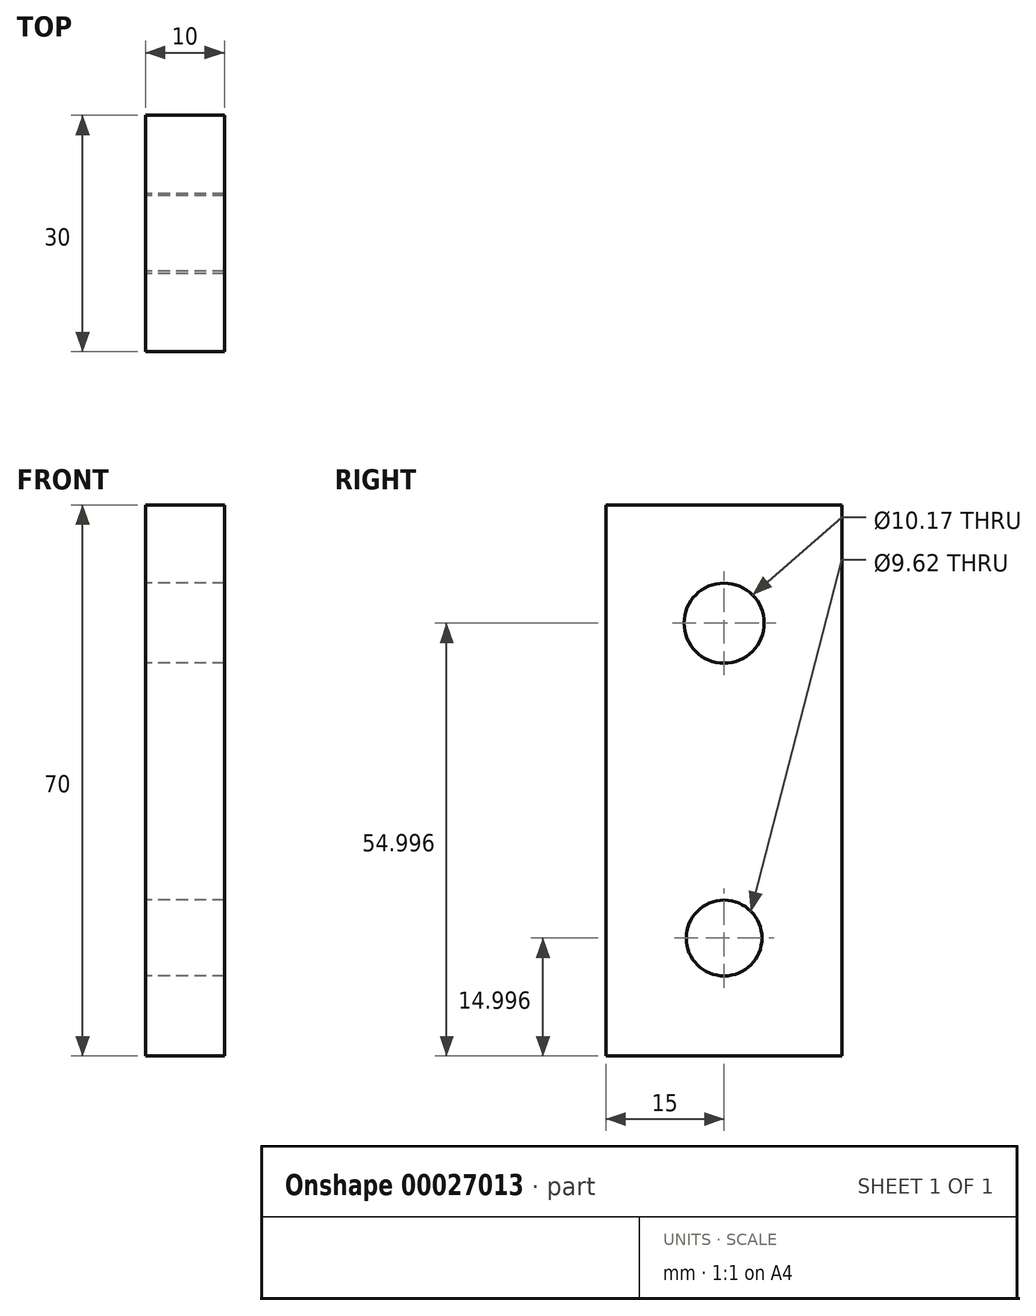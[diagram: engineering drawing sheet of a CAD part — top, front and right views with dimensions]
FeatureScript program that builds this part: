
annotation { "Feature Type Name" : "Feature", "Feature Type Description" : "" }
export const myFeature = defineFeature(function(context is Context, id is Id, definition is map)
    precondition{}
    {
        {
            var Q0;
            Q0=qCreatedBy(makeId("Right.planeOp"),FACE);
            var sketch = newSketch(context, id + "F0", { "sketchPlane" : qUnion([Q0])});
            skLineSegment(sketch, "E0.bottom", {"start": v(-15, 18.66) * mm, "end": v(15, 18.66) * mm});
            skLineSegment(sketch, "E0.top", {"start": v(-15, -51.34) * mm, "end": v(15, -51.34) * mm});
            skLineSegment(sketch, "E0.left", {"start": v(-15, 18.66) * mm, "end": v(-15, -51.34) * mm});
            skLineSegment(sketch, "E0.right", {"start": v(15, 18.66) * mm, "end": v(15, -51.34) * mm});
            skCircle(sketch, "E1", {"center": v(0, 3.66) * mm, "radius": 5.09 * mm});
            skCircle(sketch, "E2", {"center": v(0, -36.34) * mm, "radius": 4.8 * mm});
            skSolve(sketch);
        }
        {
            var Q0;
            Q0=makeQuery(id+"F0.imprint","IMPRINT",FACE,{"disambiguationData":[TD([[makeQuery(id+"F0.imprint","IMPRINT",EDGE,{"derivedFrom":sQuery(id+"F0.wireOp",EDGE,"E0.bottom")}),-1.0]])]});
            extrude(context, id + "F1", {"entities" : qUnion([Q0]), "depth" : 10 * mm});
        }
    });
